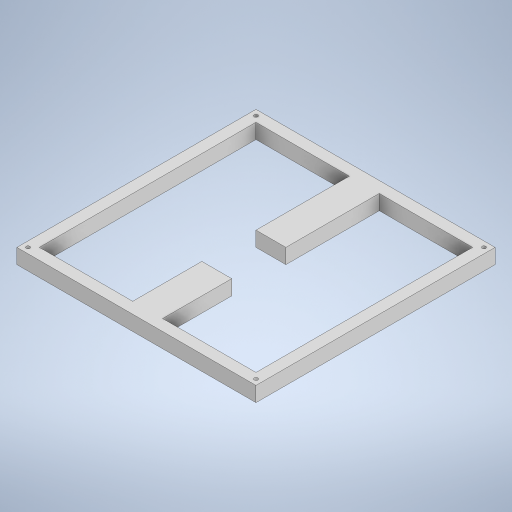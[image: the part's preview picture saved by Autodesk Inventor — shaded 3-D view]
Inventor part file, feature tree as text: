
AUTODESK INVENTOR PART (.ipt)
format: ipt  version: 2023 (Build 270158000, 158)  size: 291,328 bytes
history: native  units: in
note: dims shown in document units (in); Inventor stores cm internally (conversion verified against a paired STEP export)
features: sketch x3, extrude x2, projected_geometry x2
ambient origin geometry x8: Origin, YZ Plane, XZ Plane, XY Plane, X Axis, Y Axis, Z Axis, Center Point
bodies: Solid1 (feature_tree)
feature tree (7):
  extrude  "Extrusion1"  Depth=4.0in
  extrude  "Extrusion2"  Depth=0.25in TaperAngle=0.0deg
  sketch  "Sketch3"  dims[d13=0.5in d14=1.5625in d15=1.1562in d16=0.5in d17=0.9063in d18=0.25in d20=0.0625in d21=0.0938in d22=0.0938in d23=0.7874in d25=3.8125in d26=0.7874in d28=3.8125in d31=0.25in d32=0.0in]
  sketch  "Sketch1"  dims[d0=4.0in d1=4.0in]
  sketch  "Sketch2"  dims[d2=0.1875in d11=0.25in d12=0.0in]
  projected_geometry  "Projected Loop1"
  projected_geometry  "Projected Loop2"
